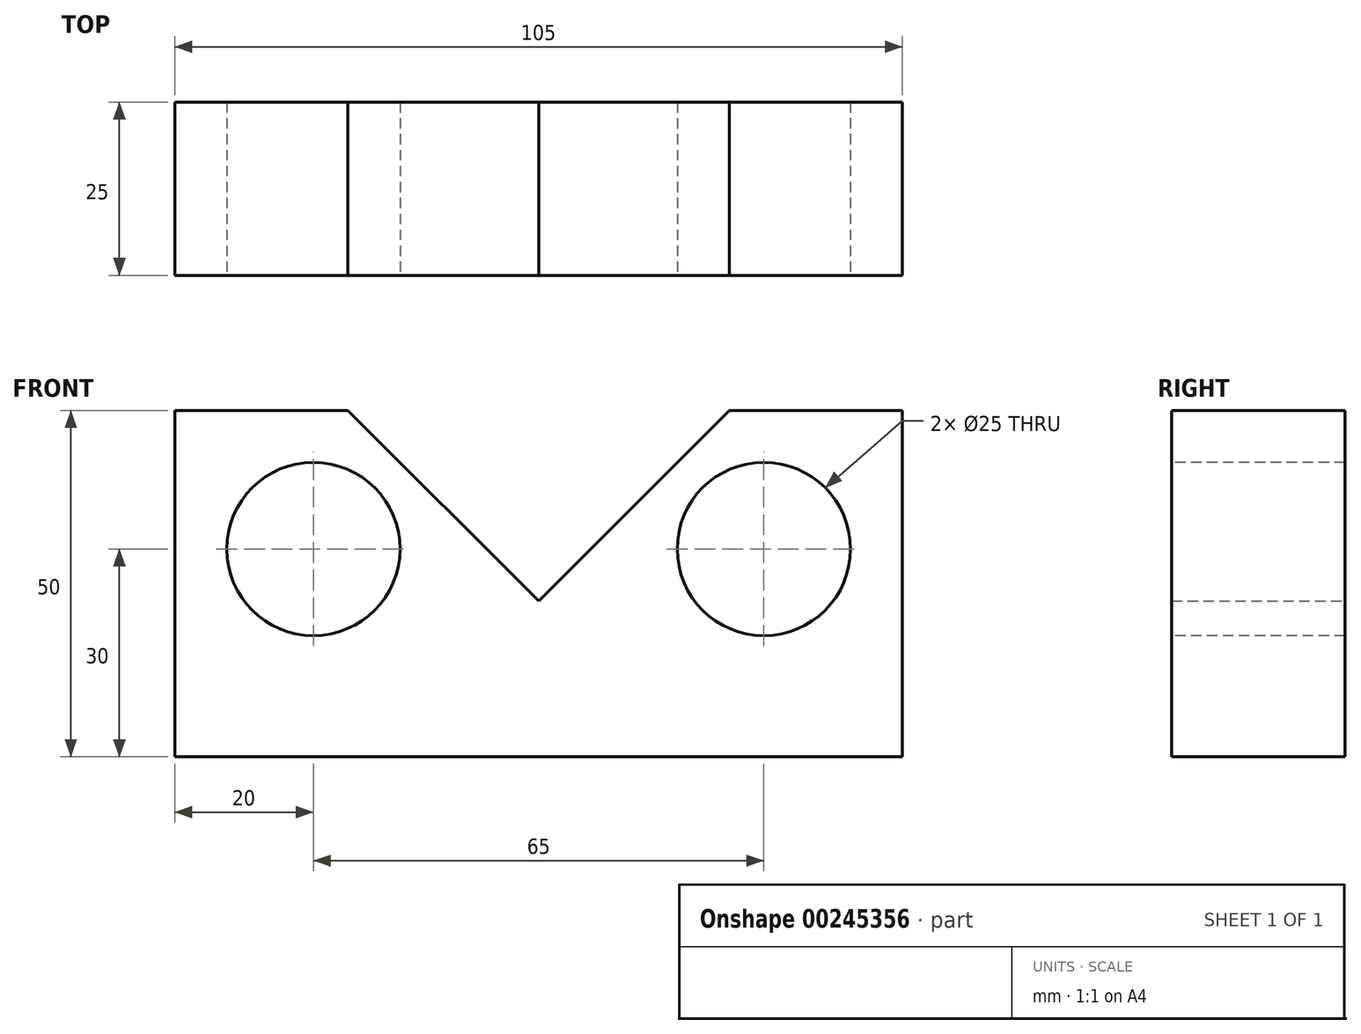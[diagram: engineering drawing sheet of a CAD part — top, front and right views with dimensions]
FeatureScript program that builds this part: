
annotation { "Feature Type Name" : "Feature", "Feature Type Description" : "" }
export const myFeature = defineFeature(function(context is Context, id is Id, definition is map)
    precondition{}
    {
        {
            var Q0;
            Q0=qCreatedBy(makeId("Front.planeOp"),FACE);
            var sketch = newSketch(context, id + "F0", { "sketchPlane" : qUnion([Q0])});
            skLineSegment(sketch, "E0", {"start": v(0, 0) * mm, "end": v(105, 0) * mm});
            skLineSegment(sketch, "E1", {"start": v(105, 0) * mm, "end": v(105, 50) * mm});
            skLineSegment(sketch, "E2", {"start": v(105, 50) * mm, "end": v(80, 50) * mm});
            skLineSegment(sketch, "E3", {"start": v(80, 50) * mm, "end": v(52.5, 22.5) * mm});
            skPoint(sketch, "E3.endSnap0", {"position": v(52.5, 0) * mm});
            skLineSegment(sketch, "E4", {"start": v(52.5, 22.5) * mm, "end": v(25, 50) * mm});
            skLineSegment(sketch, "E5", {"start": v(25, 50) * mm, "end": v(0, 50) * mm});
            skLineSegment(sketch, "E6", {"start": v(0, 50) * mm, "end": v(0, 0) * mm});
            skSolve(sketch);
        }
        {
            var Q0;
            Q0=makeQuery(id+"F0.imprint","IMPRINT",FACE,{"disambiguationData":[TD([[makeQuery(id+"F0.imprint","IMPRINT",EDGE,{"derivedFrom":sQuery(id+"F0.wireOp",EDGE,"E0")}),1.0]])]});
            extrude(context, id + "F1", {"entities" : qUnion([Q0]), "depth" : 25 * mm});
        }
        {
            var Q0;
            Q0=makeQuery(id+"F1.opExtrude","CAP_FACE",FACE,{"disambiguationData":[OSD([sQuery(id+"F0.wireOp",EDGE,"E0"),sQuery(id+"F0.wireOp",EDGE,"E1"),sQuery(id+"F0.wireOp",EDGE,"E2"),sQuery(id+"F0.wireOp",EDGE,"E3"),sQuery(id+"F0.wireOp",EDGE,"E4"),sQuery(id+"F0.wireOp",EDGE,"E5"),sQuery(id+"F0.wireOp",EDGE,"E6")])],"isStart":false});
            var sketch = newSketch(context, id + "F2", { "sketchPlane" : qUnion([Q0])});
            skCircle(sketch, "E7", {"center": v(20, 30) * mm, "radius": 12.5 * mm});
            skCircle(sketch, "E8", {"center": v(85, 30) * mm, "radius": 12.5 * mm});
            skSolve(sketch);
        }
        {
            var Q0;
            Q0=makeQuery(id+"F2.imprint","IMPRINT",FACE,{"disambiguationData":[TD([[makeQuery(id+"F2.imprint","IMPRINT",EDGE,{"derivedFrom":sQuery(id+"F2.wireOp",EDGE,"E7")}),1.0]])]});
            var Q1;
            Q1=makeQuery(id+"F2.imprint","IMPRINT",FACE,{"disambiguationData":[TD([[makeQuery(id+"F2.imprint","IMPRINT",EDGE,{"derivedFrom":sQuery(id+"F2.wireOp",EDGE,"E8")}),1.0]])]});
            extrude(context, id + "F3", {"entities" : qUnion([Q0, Q1]), "operationType" : NewBodyOperationType.REMOVE, "endBound" : BoundingType.THROUGH_ALL, "oppositeDirection" : true, "depth" : 25 * mm});
        }
    });
